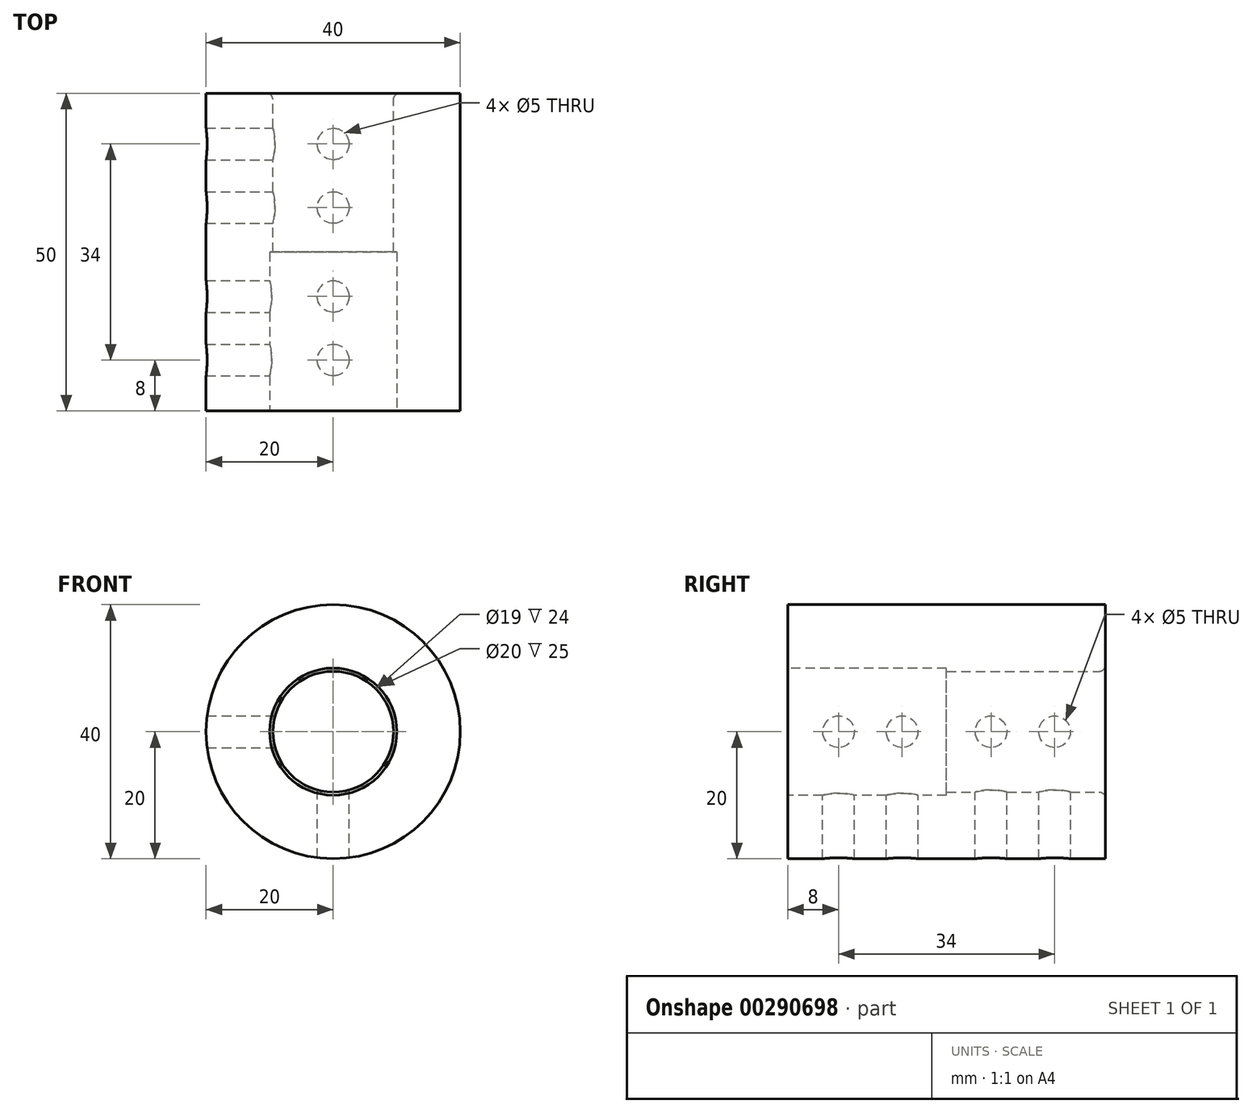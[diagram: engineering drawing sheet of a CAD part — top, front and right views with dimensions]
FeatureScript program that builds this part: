
annotation { "Feature Type Name" : "Feature", "Feature Type Description" : "" }
export const myFeature = defineFeature(function(context is Context, id is Id, definition is map)
    precondition{}
    {
        {
            var Q0;
            Q0=qCreatedBy(makeId("Front.planeOp"),FACE);
            var sketch = newSketch(context, id + "F0", { "sketchPlane" : qUnion([Q0])});
            skCircle(sketch, "E0", {"center": v(0, 0) * mm, "radius": 20 * mm});
            skCircle(sketch, "E1", {"center": v(0, 0) * mm, "radius": 9.5 * mm});
            skSolve(sketch);
        }
        {
            var Q0;
            Q0 = qSketchRegion(id + "F0", true);
            extrude(context, id + "F1", {"entities" : qUnion([Q0]), "depth" : 50 * mm});
        }
        {
            var Q0;
            Q0=makeQuery(id+"F1.opExtrude","CAP_FACE",FACE,{"disambiguationData":[OSD([sQuery(id+"F0.wireOp",EDGE,"E0"),sQuery(id+"F0.wireOp",EDGE,"E1")])],"isStart":false});
            var sketch = newSketch(context, id + "F2", { "sketchPlane" : qUnion([Q0])});
            skCircle(sketch, "E2", {"center": v(0, 0) * mm, "radius": 10 * mm});
            skSolve(sketch);
        }
        {
            var Q0;
            Q0 = qSketchRegion(id + "F2", true);
            extrude(context, id + "F3", {"entities" : qUnion([Q0]), "operationType" : NewBodyOperationType.REMOVE, "oppositeDirection" : true, "depth" : 25 * mm});
        }
        {
            var Q0;
            Q0=qCreatedBy(makeId("Right.planeOp"),FACE);
            var sketch = newSketch(context, id + "F4", { "sketchPlane" : qUnion([Q0])});
            skCircle(sketch, "E3", {"center": v(-42, 0) * mm, "radius": 2.5 * mm});
            skCircle(sketch, "E4", {"center": v(-32, 0) * mm, "radius": 2.5 * mm});
            skCircle(sketch, "E5", {"center": v(-18, 0) * mm, "radius": 2.5 * mm});
            skCircle(sketch, "E6", {"center": v(-8, 0) * mm, "radius": 2.5 * mm});
            skSolve(sketch);
        }
        {
            var Q0;
            Q0=sQuery(id+"F4.wireOp",VERTEX,"E3.center");
            var Q1;
            Q1=sQuery(id+"F4.wireOp",VERTEX,"E4.center");
            var Q2;
            Q2=sQuery(id+"F4.wireOp",VERTEX,"E5.center");
            var Q3;
            Q3=sQuery(id+"F4.wireOp",VERTEX,"E6.center");
            var Q4;
            Q4=makeQuery(id+"F1.opExtrude","SWEPT_BODY",BODY,{"disambiguationData":[OSD([sQuery(id+"F0.wireOp",EDGE,"E0"),sQuery(id+"F0.wireOp",EDGE,"E1")])]});
            hole(context, id + "F5", {"style" : HoleStyle.SIMPLE, "endStyle" : HoleEndStyle.BLIND, "standardTappedOrClearance" : lookupTablePath({ "standard" : "ISO", "engagement" : "75%", "pitch" : "1 mm", "size" : "M6", "type" : "Tapped" }), "standardBlindInLast" : lookupTablePath({ "standard" : "ISO", "engagement" : "75%", "pitch" : "1 mm", "size" : "M6", "type" : "Tapped" }), "holeDiameter" : 5 * mm, "showTappedDepth" : true, "holeDepth" : 50 * mm, "tappedDepth" : 47 * mm, "tapClearance" : 3, "startFromSketch" : true, "locations" : qUnion([Q0, Q1, Q2, Q3]), "scope" : qUnion([Q4]), "majorDiameter" : 6 * mm});
        }
        {
            var Q0;
            Q0=qCreatedBy(makeId("Top.planeOp"),FACE);
            var sketch = newSketch(context, id + "F6", { "sketchPlane" : qUnion([Q0])});
            skCircle(sketch, "E7", {"center": v(0, -8) * mm, "radius": 2.5 * mm});
            skCircle(sketch, "E8", {"center": v(0, -18) * mm, "radius": 2.5 * mm});
            skCircle(sketch, "E9", {"center": v(0, -32) * mm, "radius": 2.5 * mm});
            skCircle(sketch, "E10", {"center": v(0, -42) * mm, "radius": 2.5 * mm});
            skSolve(sketch);
        }
        {
            var Q0;
            Q0=sQuery(id+"F6.wireOp",VERTEX,"E7.center");
            var Q1;
            Q1=sQuery(id+"F6.wireOp",VERTEX,"E8.center");
            var Q2;
            Q2=sQuery(id+"F6.wireOp",VERTEX,"E9.center");
            var Q3;
            Q3=sQuery(id+"F6.wireOp",VERTEX,"E10.center");
            var Q4;
            Q4=makeQuery(id+"F1.opExtrude","SWEPT_BODY",BODY,{"disambiguationData":[OSD([sQuery(id+"F0.wireOp",EDGE,"E0"),sQuery(id+"F0.wireOp",EDGE,"E1")])]});
            hole(context, id + "F7", {"style" : HoleStyle.SIMPLE, "endStyle" : HoleEndStyle.BLIND, "standardTappedOrClearance" : lookupTablePath({ "standard" : "ISO", "engagement" : "75%", "pitch" : "1 mm", "size" : "M6", "type" : "Tapped" }), "standardBlindInLast" : lookupTablePath({ "standard" : "ISO", "engagement" : "75%", "pitch" : "1 mm", "size" : "M6", "type" : "Tapped" }), "holeDiameter" : 5 * mm, "showTappedDepth" : true, "holeDepth" : 50 * mm, "tappedDepth" : 47 * mm, "tapClearance" : 3, "startFromSketch" : true, "locations" : qUnion([Q0, Q1, Q2, Q3]), "scope" : qUnion([Q4]), "majorDiameter" : 6 * mm});
        }
        {
            var Q0;
            Q0=makeQuery(id+"F1.opExtrude","CAP_EDGE",EDGE,{"disambiguationData":[OSD([sQuery(id+"F0.wireOp",EDGE,"E1")])],"isStart":true});
            var Q1;
            Q1=makeQuery(id+"F3.boolean.opBoolean","COPY",EDGE,{"derivedFrom":makeQuery(id+"F3.opExtrude","CAP_EDGE",EDGE,{"disambiguationData":[OSD([sQuery(id+"F2.wireOp",EDGE,"E2")])],"isStart":true})});
            fillet(context, id + "F8", {"entities" : qUnion([Q0, Q1]), "radius" : 1 * mm, "tangentPropagation" : true, "allowEdgeOverflow" : false});
        }
    });
